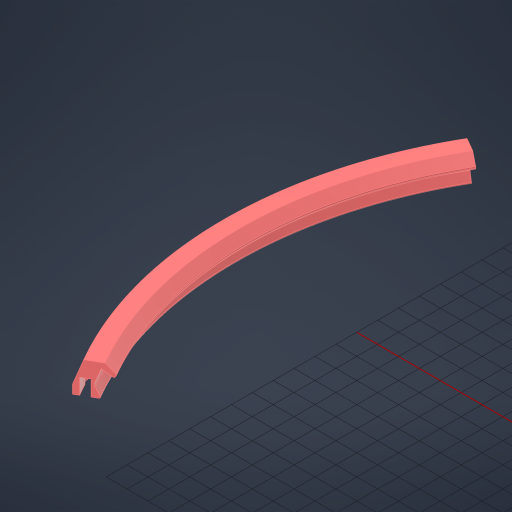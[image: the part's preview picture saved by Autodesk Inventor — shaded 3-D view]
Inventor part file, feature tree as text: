
AUTODESK INVENTOR PART (.ipt)
format: ipt  version: 2023.2 (Build 272271030, 271C)  size: 357,888 bytes
history: native  units: mm
features: sketch x2, revolve x2, hole x1, extrude x1, projected_geometry x1
ambient origin geometry x8: Origin, YZ Plane, XZ Plane, XY Plane, X Axis, Y Axis, Z Axis, Center Point
bodies: Volumenkörper1 (feature_tree)
feature tree (7):
  sketch  "Skizze1"  dims[d1=30.0mm d5=1.0mm]
  revolve  "Umdrehung1"
  revolve  "Umdrehung2"
  sketch  "Skizze2"  dims[d9=135.0deg d14=8.5mm d18=360.0mm d25=50.0mm d26=225.0mm d30=60.0deg d31=15.0mm d40=3.5mm d41=120.0mm d42=35.0mm d43=1.0mm d47=6.0mm d50=11.362634mm d54=15.0mm d59=2.094395mm d60=27.925268mm d66=15.0mm d70=4.5mm d71=6.0mm d73=3.2mm d74=3.0mm d75=6.0mm d76=6.0mm d77=6.0mm d79=4.5mm d80=15.0mm d81=2.0mm d82=8.0mm d83=120.0mm d84=30.0deg d85=0.436332mm d86=1.745329mm d87=0.436332mm d88=1.745329mm d89=4.5mm d90=4.5mm d91=6.0mm d92=4.0mm d93=2.0mm d94=90.0deg d95=6.0mm d96=0.0mm d97=10.0mm d98=0.0mm d99=0.0mm]
  hole  "Bohrung1"  [1 undecoded]
  extrude  "Extrusion1"  Depth=10.0mm
  projected_geometry  "Projizierte Kontur1"
note: 1 required parameter value undecoded (feature->parameter linkage not recoverable at this tier; creation-order binding heuristic only, values carry confidence <= 0.55)
